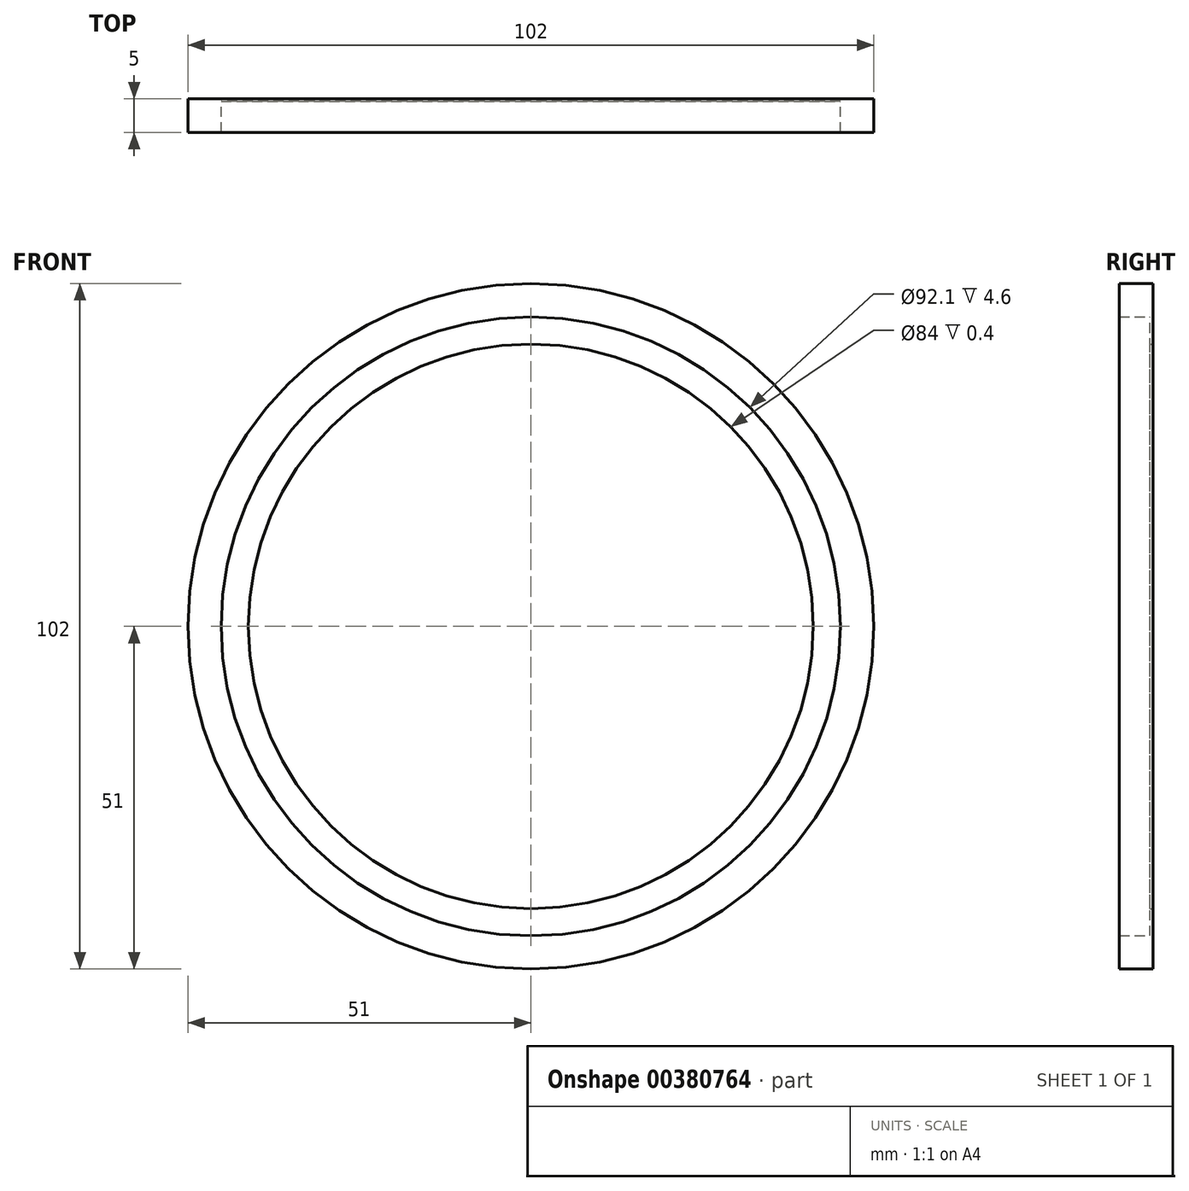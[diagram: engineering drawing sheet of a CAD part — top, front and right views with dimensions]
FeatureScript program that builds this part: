
annotation { "Feature Type Name" : "Feature", "Feature Type Description" : "" }
export const myFeature = defineFeature(function(context is Context, id is Id, definition is map)
    precondition{}
    {
        {
            var Q0;
            Q0=qCreatedBy(makeId("Front.planeOp"),FACE);
            var sketch = newSketch(context, id + "F0", { "sketchPlane" : qUnion([Q0])});
            skCircle(sketch, "E0", {"center": v(0, 0) * mm, "radius": 46.05 * mm});
            skCircle(sketch, "E1", {"center": v(0, 0) * mm, "radius": 51 * mm});
            skSolve(sketch);
        }
        {
            var Q0;
            Q0=makeQuery(id+"F0.imprint","IMPRINT",FACE,{"disambiguationData":[TD([[makeQuery(id+"F0.imprint","IMPRINT",EDGE,{"derivedFrom":sQuery(id+"F0.wireOp",EDGE,"E0")}),-1.0]])]});
            extrude(context, id + "F1", {"entities" : qUnion([Q0]), "depth" : 5 * mm});
        }
        {
            var Q0;
            Q0=makeQuery(id+"F0.imprint","IMPRINT",FACE,{"disambiguationData":[TD([[makeQuery(id+"F0.imprint","IMPRINT",EDGE,{"derivedFrom":sQuery(id+"F0.wireOp",EDGE,"E0")}),1.0]])]});
            extrude(context, id + "F2", {"entities" : qUnion([Q0]), "operationType" : NewBodyOperationType.ADD, "depth" : 0.4 * mm});
        }
        {
            var Q0;
            Q0=sQuery(id+"F0.wireOp",VERTEX,"E0.center");
            var Q1;
            Q1=makeQuery(id+"F1.opExtrude","SWEPT_BODY",BODY,{"disambiguationData":[OSD([sQuery(id+"F0.wireOp",EDGE,"E0"),sQuery(id+"F0.wireOp",EDGE,"E1")])]});
            hole(context, id + "F3", {"style" : HoleStyle.SIMPLE, "endStyle" : HoleEndStyle.THROUGH, "oppositeDirection" : true, "holeDiameter" : 84 * mm, "tappedDepth" : 12 * mm, "tapClearance" : 3, "startFromSketch" : true, "locations" : qUnion([Q0]), "scope" : qUnion([Q1])});
        }
    });
